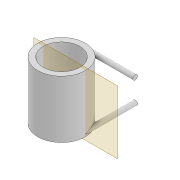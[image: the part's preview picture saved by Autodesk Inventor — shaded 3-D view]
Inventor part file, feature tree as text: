
AUTODESK INVENTOR PART (.ipt)
format: ipt  version: 2022 (Build 260153000, 153)  size: 116,224 bytes
history: native  units: mm
features: extrude x3, sketch x3, projected_geometry x2
ambient origin geometry x8: Origin, YZ Plane, XZ Plane, XY Plane, X Axis, Y Axis, Z Axis, Center Point
bodies: Solid1 (feature_tree)
feature tree (8):
  extrude  "Extrusion1"  Depth=7.0mm
  extrude  "Extrusion2"  Depth=10.0mm TaperAngle=0.0deg
  extrude  "Extrusion3"  Depth=10.0mm
  sketch  "Sketch1"  dims[d0=9.1mm d1=7.0mm]
  sketch  "Sketch2"  dims[d2=11.0mm d3=0.0mm d5=10.0mm d6=0.0mm]
  projected_geometry  "Projected Loop1"
  sketch  "Sketch3"  dims[d8=10.0mm d9=0.0mm d11=0.9mm d12=0.9mm]
  projected_geometry  "Projected Loop2"
